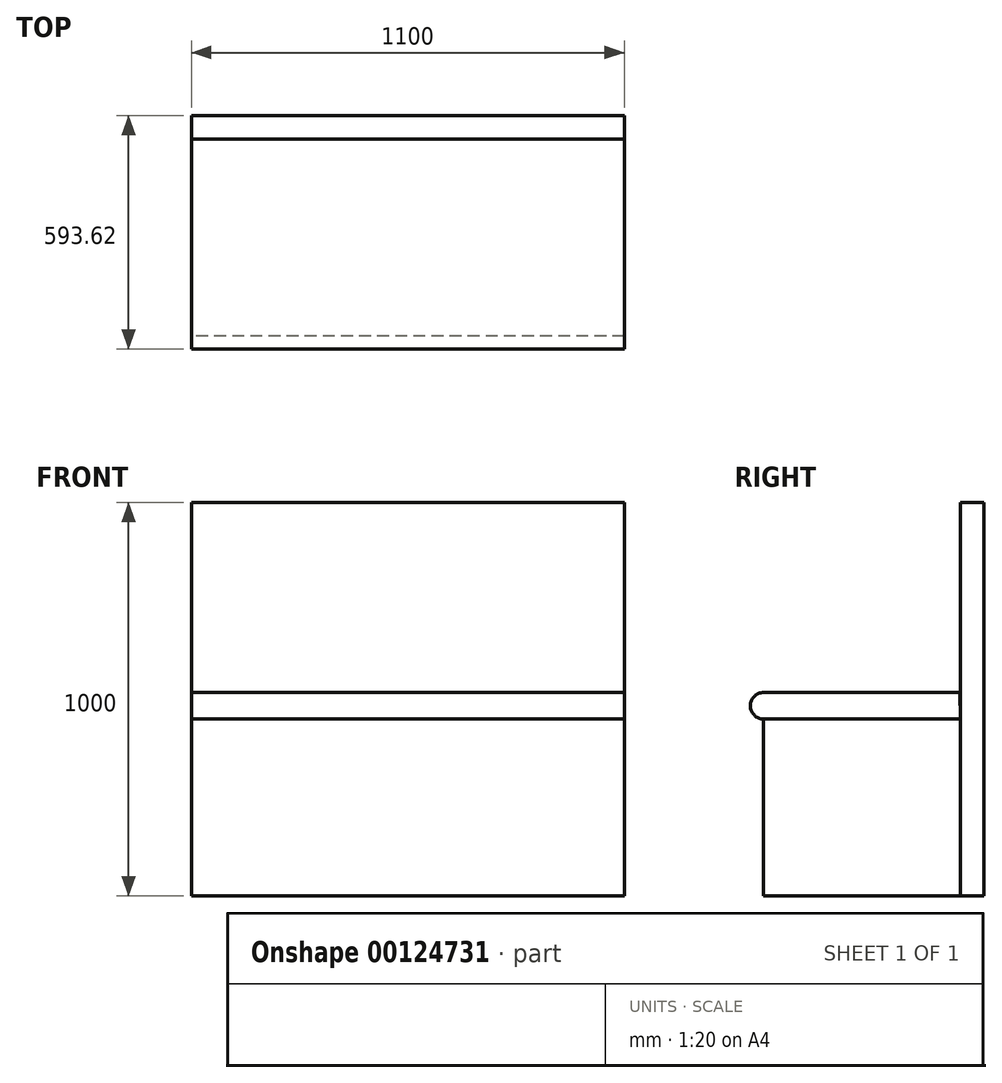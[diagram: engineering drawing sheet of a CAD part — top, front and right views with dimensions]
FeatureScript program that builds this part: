
annotation { "Feature Type Name" : "Feature", "Feature Type Description" : "" }
export const myFeature = defineFeature(function(context is Context, id is Id, definition is map)
    precondition{}
    {
        {
            var Q0;
            Q0=qCreatedBy(makeId("Right.planeOp"),FACE);
            var sketch = newSketch(context, id + "F0", { "sketchPlane" : qUnion([Q0])});
            skLineSegment(sketch, "E0.bottom", {"start": v(-235.3, -227.93) * mm, "end": v(264.7, -227.93) * mm});
            skLineSegment(sketch, "E0.top", {"start": v(-235.3, 222.07) * mm, "end": v(264.7, 222.07) * mm});
            skLineSegment(sketch, "E0.left", {"start": v(-235.3, -227.93) * mm, "end": v(-235.3, 222.07) * mm});
            skLineSegment(sketch, "E0.right", {"start": v(264.7, -227.93) * mm, "end": v(264.7, 222.07) * mm});
            skSolve(sketch);
        }
        {
            var Q0;
            Q0 = qSketchRegion(id + "F0", true);
            extrude(context, id + "F1", {"entities" : qUnion([Q0]), "depth" : 1100 * mm});
        }
        {
            var Q0;
            Q0=makeQuery(id+"F1.opExtrude","CAP_FACE",FACE,{"disambiguationData":[OSD([sQuery(id+"F0.wireOp",EDGE,"E0.bottom"),sQuery(id+"F0.wireOp",EDGE,"E0.top"),sQuery(id+"F0.wireOp",EDGE,"E0.left"),sQuery(id+"F0.wireOp",EDGE,"E0.right")])],"isStart":false});
            var sketch = newSketch(context, id + "F2", { "sketchPlane" : qUnion([Q0])});
            skArc(sketch, "E1", {"start": v(-235.3, 289.31) * mm, "mid": v(-268.92, 255.7) * mm, "end": v(-235.3, 222.07) * mm});
            skLineSegment(sketch, "E2", {"start": v(-235.3, 289.31) * mm, "end": v(263.9, 289.31) * mm});
            skLineSegment(sketch, "E3", {"start": v(263.9, 289.31) * mm, "end": v(264.7, 222.07) * mm});
            skSolve(sketch);
        }
        {
            var Q0;
            Q0 = qSketchRegion(id + "F2", true);
            var Q1;
            Q1=makeQuery(id+"F2.imprint","IMPRINT",FACE,{"disambiguationData":[TD([[makeQuery(id+"F2.imprint","IMPRINT",EDGE,{"derivedFrom":sQuery(id+"F2.wireOp",EDGE,"E1")}),1.0]])]});
            extrude(context, id + "F3", {"entities" : qUnion([Q0, Q1]), "oppositeDirection" : true, "depth" : 1100 * mm});
        }
        {
            var Q0;
            {var subQ0=sQuery(id+"F0.wireOp",EDGE,"E0.top");Q0=makeQuery(id+"F3.boolean.opBoolean","MERGE",FACE,{"derivedFrom":[makeQuery(id+"F1.opExtrude","CAP_FACE",FACE,{"disambiguationData":[OSD([sQuery(id+"F0.wireOp",EDGE,"E0.bottom"),subQ0,sQuery(id+"F0.wireOp",EDGE,"E0.left"),sQuery(id+"F0.wireOp",EDGE,"E0.right")])],"isStart":false}),makeQuery(id+"F3.opExtrude","CAP_FACE",FACE,{"disambiguationData":[OSD([subQ0,sQuery(id+"F2.wireOp",EDGE,"E1"),sQuery(id+"F2.wireOp",EDGE,"E2"),sQuery(id+"F2.wireOp",EDGE,"E3")])],"isStart":true})]});}
            var sketch = newSketch(context, id + "F4", { "sketchPlane" : qUnion([Q0])});
            skLineSegment(sketch, "E4.bottom", {"start": v(264.7, -227.93) * mm, "end": v(324.7, -227.93) * mm});
            skLineSegment(sketch, "E4.top", {"start": v(264.7, 772.07) * mm, "end": v(324.7, 772.07) * mm});
            skLineSegment(sketch, "E4.left", {"start": v(264.7, -227.93) * mm, "end": v(264.7, 772.07) * mm});
            skLineSegment(sketch, "E4.right", {"start": v(324.7, -227.93) * mm, "end": v(324.7, 772.07) * mm});
            skSolve(sketch);
        }
        {
            var Q0;
            Q0 = qSketchRegion(id + "F4", true);
            var Q1;
            {var subQ3=sQuery(id+"F4.wireOp",EDGE,"E4.bottom");Q1=makeQuery(id+"F4.imprint","IMPRINT",FACE,{"disambiguationData":[TD([[makeQuery(id+"F4.imprint","IMPRINT",EDGE,{"derivedFrom":subQ3}),1.0]])]});}
            extrude(context, id + "F5", {"entities" : qUnion([Q0, Q1]), "oppositeDirection" : true, "depth" : 1100 * mm});
        }
    });
